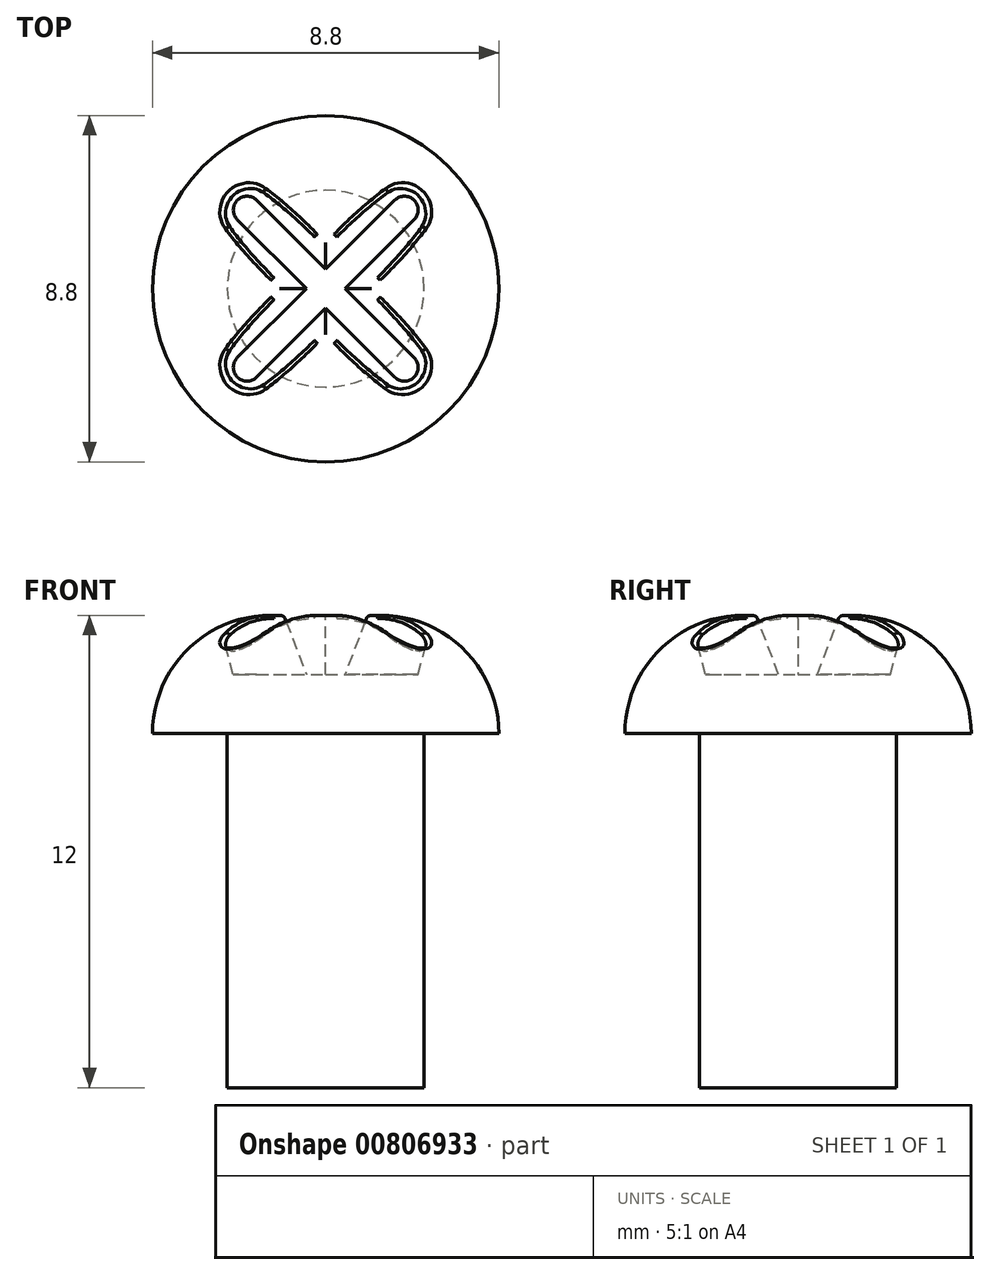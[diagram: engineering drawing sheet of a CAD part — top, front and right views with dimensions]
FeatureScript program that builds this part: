
annotation { "Feature Type Name" : "Feature", "Feature Type Description" : "" }
export const myFeature = defineFeature(function(context is Context, id is Id, definition is map)
    precondition{}
    {
        {
            var Q0;
            Q0=qCreatedBy(makeId("Top.planeOp"),FACE);
            var sketch = newSketch(context, id + "F0", { "sketchPlane" : qUnion([Q0])});
            skCircle(sketch, "E0", {"center": v(0, 0) * mm, "radius": 2.5 * mm});
            skSolve(sketch);
        }
        {
            var Q0;
            Q0=qSketchRegion(id+"F0",true);
            extrude(context, id + "F1", {"entities" : qUnion([Q0]), "depth" : 9 * mm, "offsetDistance" : 25 * mm});
        }
        {
            var Q0;
            Q0=makeQuery(id+"F1.opExtrude","CAP_FACE",FACE,{"disambiguationData":[OSD([sQuery(id+"F0.wireOp",EDGE,"E0")])],"isStart":false});
            var sketch = newSketch(context, id + "F2", { "sketchPlane" : qUnion([Q0])});
            skCircle(sketch, "E1", {"center": v(0, 0) * mm, "radius": 4.4 * mm});
            skSolve(sketch);
        }
        {
            var Q0;
            Q0=makeQuery(id+"F2.imprint","IMPRINT",FACE,{"disambiguationData":[TD([[makeQuery(id+"F2.imprint","IMPRINT",EDGE,{"derivedFrom":sQuery(id+"F2.wireOp",EDGE,"E1")}),1.0]])]});
            var Q1;
            Q1=makeQuery(id+"F2.imprint","IMPRINT",FACE,{"disambiguationData":[TD([[makeQuery(id+"F2.imprint","IMPRINT",EDGE,{"derivedFrom":makeQuery(id+"F1.opExtrude","CAP_EDGE",EDGE,{"disambiguationData":[OSD([sQuery(id+"F0.wireOp",EDGE,"E0")])],"isStart":false})}),1.0]])]});
            extrude(context, id + "F3", {"entities" : qUnion([Q0, Q1]), "operationType" : NewBodyOperationType.ADD, "depth" : 3 * mm, "offsetDistance" : 25 * mm});
        }
        {
            var Q0;
            Q0=makeQuery(id+"F3.opExtrude","CAP_EDGE",EDGE,{"disambiguationData":[OSD([sQuery(id+"F2.wireOp",EDGE,"E1")])],"isStart":false});
            fillet(context, id + "F4", {"entities" : qUnion([Q0]), "radius" : 3 * mm, "tangentPropagation" : true, "allowEdgeOverflow" : false});
        }
        {
            var Q0;
            Q0=makeQuery(id+"F3.opExtrude","CAP_FACE",FACE,{"disambiguationData":[OSD([sQuery(id+"F2.wireOp",EDGE,"E1")])],"isStart":false});
            var sketch = newSketch(context, id + "F5", { "sketchPlane" : qUnion([Q0])});
            skLineSegment(sketch, "E2", {"start": v(-2.3, 0) * mm, "end": v(2.4, 0) * mm, "construction": true});
            skLineSegment(sketch, "E3", {"start": v(0, 2.68) * mm, "end": v(0, -2.44) * mm, "construction": true});
            skLineSegment(sketch, "E4.bottom", {"start": v(2, -2) * mm, "end": v(-2, -2) * mm, "construction": true});
            skLineSegment(sketch, "E4.top", {"start": v(2, 2) * mm, "end": v(-2, 2) * mm, "construction": true});
            skLineSegment(sketch, "E4.left", {"start": v(2, -2) * mm, "end": v(2, 2) * mm, "construction": true});
            skLineSegment(sketch, "E4.right", {"start": v(-2, -2) * mm, "end": v(-2, 2) * mm, "construction": true});
            skPoint(sketch, "E4.middle", {"position": v(0, 0) * mm});
            skLineSegment(sketch, "E5", {"start": v(-2, -2) * mm, "end": v(2, 2) * mm});
            skLineSegment(sketch, "E6", {"start": v(-2, 2) * mm, "end": v(2, -2) * mm});
            skArc(sketch, "E7.0.startCap", {"start": v(-2.53, 1.47) * mm, "mid": v(-2.53, 2.53) * mm, "end": v(-1.47, 2.53) * mm});
            skArc(sketch, "E7.0.endCap", {"start": v(2.53, -1.47) * mm, "mid": v(2.53, -2.53) * mm, "end": v(1.47, -2.53) * mm});
            skLineSegment(sketch, "E7.0.left", {"start": v(-1.47, 2.53) * mm, "end": v(2.53, -1.47) * mm});
            skLineSegment(sketch, "E7.0.right", {"start": v(-2.53, 1.47) * mm, "end": v(1.47, -2.53) * mm});
            skArc(sketch, "E7.1.startCap", {"start": v(-1.47, -2.53) * mm, "mid": v(-2.53, -2.53) * mm, "end": v(-2.53, -1.47) * mm});
            skArc(sketch, "E7.1.endCap", {"start": v(1.47, 2.53) * mm, "mid": v(2.53, 2.53) * mm, "end": v(2.53, 1.47) * mm});
            skLineSegment(sketch, "E7.1.left", {"start": v(-2.53, -1.47) * mm, "end": v(1.47, 2.53) * mm});
            skLineSegment(sketch, "E7.1.right", {"start": v(-1.47, -2.53) * mm, "end": v(2.53, 1.47) * mm});
            skSolve(sketch);
        }
        {
            var Q0;
            Q0=qSketchRegion(id+"F5",true);
            extrude(context, id + "F6", {"entities" : qUnion([Q0]), "operationType" : NewBodyOperationType.REMOVE, "oppositeDirection" : true, "depth" : 1.5 * mm, "offsetDistance" : 25 * mm, "hasDraft" : true, "draftAngle" : 15 * degree, "draftPullDirection" : true});
        }
        {
            var Q0;
            {var subQ0=sQuery(id+"F5.wireOp",EDGE,"E7.0.right");var subQ1=sQuery(id+"F2.wireOp",EDGE,"E1");Q0=makeQuery(id+"F6.boolean.opBoolean","INTERSECT",EDGE,{"derivedFrom":[makeQuery(id+"F4.opFillet","BLEND_FACE",FACE,{"disambiguationData":[OSD([subQ1])]}),makeQuery(id+"F6.opExtrude","SWEPT_FACE",FACE,{"disambiguationData":[OSD([subQ0]),TDD([makeQuery(id+"F5.imprint","IMPRINT",EDGE,{"disambiguationData":[TD([[makeQuery(id+"F5.imprint","INTERSECT",VERTEX,{"derivedFrom":[subQ0,sQuery(id+"F5.wireOp",EDGE,"E7.1.right")]}),-1.0]])],"derivedFrom":subQ0}),makeQuery(id+"F5.imprint","IMPRINT",EDGE,{"disambiguationData":[TD([[makeQuery(id+"F5.imprint","INTERSECT",VERTEX,{"derivedFrom":[sQuery(id+"F5.wireOp",EDGE,"E7.0.endCap"),subQ0]}),1.0]])],"derivedFrom":subQ0})])]})]});}
            var Q1;
            {var subQ0=sQuery(id+"F5.wireOp",EDGE,"E7.1.right");var subQ1=sQuery(id+"F2.wireOp",EDGE,"E1");Q1=makeQuery(id+"F6.boolean.opBoolean","INTERSECT",EDGE,{"derivedFrom":[makeQuery(id+"F4.opFillet","BLEND_FACE",FACE,{"disambiguationData":[OSD([subQ1])]}),makeQuery(id+"F6.opExtrude","SWEPT_FACE",FACE,{"disambiguationData":[OSD([subQ0]),TDD([makeQuery(id+"F5.imprint","IMPRINT",EDGE,{"disambiguationData":[TD([[makeQuery(id+"F5.imprint","INTERSECT",VERTEX,{"derivedFrom":[sQuery(id+"F5.wireOp",EDGE,"E7.0.left"),subQ0]}),-1.0]])],"derivedFrom":subQ0}),makeQuery(id+"F5.imprint","IMPRINT",EDGE,{"disambiguationData":[TD([[makeQuery(id+"F5.imprint","INTERSECT",VERTEX,{"derivedFrom":[sQuery(id+"F5.wireOp",EDGE,"E7.1.endCap"),subQ0]}),1.0]])],"derivedFrom":subQ0})])]})]});}
            var Q2;
            {var subQ0=sQuery(id+"F5.wireOp",EDGE,"E7.1.left");var subQ1=sQuery(id+"F2.wireOp",EDGE,"E1");Q2=makeQuery(id+"F6.boolean.opBoolean","INTERSECT",EDGE,{"derivedFrom":[makeQuery(id+"F4.opFillet","BLEND_FACE",FACE,{"disambiguationData":[OSD([subQ1])]}),makeQuery(id+"F6.opExtrude","SWEPT_FACE",FACE,{"disambiguationData":[OSD([subQ0]),TDD([makeQuery(id+"F5.imprint","IMPRINT",EDGE,{"disambiguationData":[TD([[makeQuery(id+"F5.imprint","INTERSECT",VERTEX,{"derivedFrom":[sQuery(id+"F5.wireOp",EDGE,"E7.0.left"),subQ0]}),-1.0]])],"derivedFrom":subQ0}),makeQuery(id+"F5.imprint","IMPRINT",EDGE,{"disambiguationData":[TD([[makeQuery(id+"F5.imprint","INTERSECT",VERTEX,{"derivedFrom":[sQuery(id+"F5.wireOp",EDGE,"E7.1.endCap"),subQ0]}),1.0]])],"derivedFrom":subQ0})])]})]});}
            var Q3;
            {var subQ0=sQuery(id+"F5.wireOp",EDGE,"E7.0.left");var subQ1=sQuery(id+"F2.wireOp",EDGE,"E1");Q3=makeQuery(id+"F6.boolean.opBoolean","INTERSECT",EDGE,{"derivedFrom":[makeQuery(id+"F4.opFillet","BLEND_FACE",FACE,{"disambiguationData":[OSD([subQ1])]}),makeQuery(id+"F6.opExtrude","SWEPT_FACE",FACE,{"disambiguationData":[OSD([subQ0]),TDD([makeQuery(id+"F5.imprint","IMPRINT",EDGE,{"disambiguationData":[TD([[makeQuery(id+"F5.imprint","INTERSECT",VERTEX,{"derivedFrom":[sQuery(id+"F5.wireOp",EDGE,"E7.0.startCap"),subQ0]}),-1.0]])],"derivedFrom":subQ0}),makeQuery(id+"F5.imprint","IMPRINT",EDGE,{"disambiguationData":[TD([[makeQuery(id+"F5.imprint","INTERSECT",VERTEX,{"derivedFrom":[subQ0,sQuery(id+"F5.wireOp",EDGE,"E7.1.left")]}),1.0]])],"derivedFrom":subQ0})])]})]});}
            var Q4;
            {var subQ0=sQuery(id+"F5.wireOp",EDGE,"E7.1.left");var subQ1=sQuery(id+"F2.wireOp",EDGE,"E1");Q4=makeQuery(id+"F6.boolean.opBoolean","INTERSECT",EDGE,{"derivedFrom":[makeQuery(id+"F4.opFillet","BLEND_FACE",FACE,{"disambiguationData":[OSD([subQ1])]}),makeQuery(id+"F6.opExtrude","SWEPT_FACE",FACE,{"disambiguationData":[OSD([subQ0]),TDD([makeQuery(id+"F5.imprint","IMPRINT",EDGE,{"disambiguationData":[TD([[makeQuery(id+"F5.imprint","INTERSECT",VERTEX,{"derivedFrom":[sQuery(id+"F5.wireOp",EDGE,"E7.1.startCap"),subQ0]}),-1.0]])],"derivedFrom":subQ0}),makeQuery(id+"F5.imprint","IMPRINT",EDGE,{"disambiguationData":[TD([[makeQuery(id+"F5.imprint","INTERSECT",VERTEX,{"derivedFrom":[sQuery(id+"F5.wireOp",EDGE,"E7.0.right"),subQ0]}),1.0]])],"derivedFrom":subQ0})])]})]});}
            fillet(context, id + "F7", {"entities" : qUnion([Q0, Q1, Q2, Q3, Q4]), "radius" : 0.1 * mm, "tangentPropagation" : true, "allowEdgeOverflow" : false});
        }
    });
